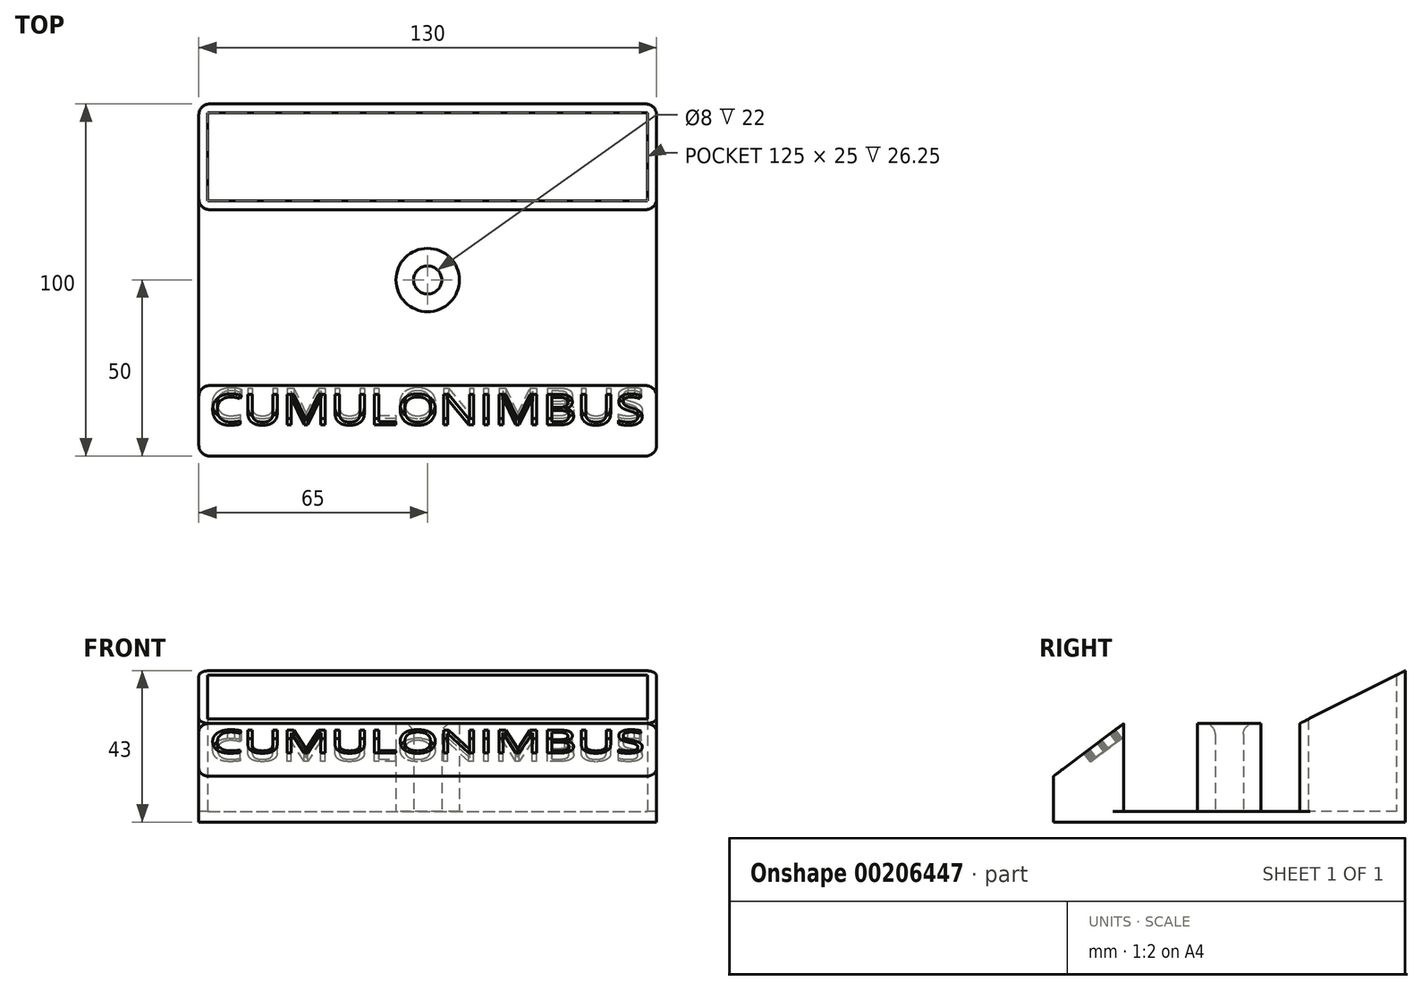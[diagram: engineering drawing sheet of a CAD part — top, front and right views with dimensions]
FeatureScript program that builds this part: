
annotation { "Feature Type Name" : "Feature", "Feature Type Description" : "" }
export const myFeature = defineFeature(function(context is Context, id is Id, definition is map)
    precondition{}
    {
        {
            var Q0;
            Q0=qCreatedBy(makeId("Top.planeOp"),FACE);
            var sketch = newSketch(context, id + "F0", { "sketchPlane" : qUnion([Q0])});
            skLineSegment(sketch, "E0.bottom", {"start": v(-65, 100) * mm, "end": v(65, 100) * mm});
            skLineSegment(sketch, "E0.top", {"start": v(-65, 0) * mm, "end": v(65, 0) * mm});
            skLineSegment(sketch, "E0.left", {"start": v(65, 100) * mm, "end": v(65, 0) * mm});
            skLineSegment(sketch, "E0.right", {"start": v(-65, 100) * mm, "end": v(-65, 0) * mm});
            skSolve(sketch);
        }
        {
            var Q0;
            Q0=makeQuery(id+"F0.imprint","IMPRINT",FACE,{"disambiguationData":[TD([[makeQuery(id+"F0.imprint","IMPRINT",EDGE,{"derivedFrom":sQuery(id+"F0.wireOp",EDGE,"E0.bottom")}),-1.0]])]});
            extrude(context, id + "F1", {"entities" : qUnion([Q0]), "depth" : 3 * mm});
        }
        {
            var Q0;
            Q0=makeQuery(id+"F1.opExtrude","CAP_FACE",FACE,{"disambiguationData":[OSD([sQuery(id+"F0.wireOp",EDGE,"E0.bottom"),sQuery(id+"F0.wireOp",EDGE,"E0.top"),sQuery(id+"F0.wireOp",EDGE,"E0.left"),sQuery(id+"F0.wireOp",EDGE,"E0.right")])],"isStart":false});
            var sketch = newSketch(context, id + "F2", { "sketchPlane" : qUnion([Q0])});
            skLineSegment(sketch, "E1", {"start": v(0, 0) * mm, "end": v(0, 100) * mm, "construction": true});
            skCircle(sketch, "E2", {"center": v(0, 50) * mm, "radius": 9 * mm});
            skCircle(sketch, "E3", {"center": v(0, 50) * mm, "radius": 4 * mm});
            skLineSegment(sketch, "E4.bottom", {"start": v(-65, 0) * mm, "end": v(65, 0) * mm});
            skLineSegment(sketch, "E4.top", {"start": v(-65, 20) * mm, "end": v(65, 20) * mm});
            skLineSegment(sketch, "E4.left", {"start": v(-65, 0) * mm, "end": v(-65, 20) * mm});
            skLineSegment(sketch, "E4.right", {"start": v(65, 0) * mm, "end": v(65, 20) * mm});
            skLineSegment(sketch, "E5.bottom", {"start": v(-65, 100) * mm, "end": v(65, 100) * mm});
            skLineSegment(sketch, "E5.top", {"start": v(-65, 70) * mm, "end": v(65, 70) * mm});
            skLineSegment(sketch, "E5.left", {"start": v(-65, 100) * mm, "end": v(-65, 70) * mm});
            skLineSegment(sketch, "E5.right", {"start": v(65, 100) * mm, "end": v(65, 70) * mm});
            skLineSegment(sketch, "E6.0", {"start": v(62.5, 97.5) * mm, "end": v(62.5, 72.5) * mm});
            skLineSegment(sketch, "E6.1", {"start": v(-62.5, 97.5) * mm, "end": v(62.5, 97.5) * mm});
            skLineSegment(sketch, "E6.2", {"start": v(-62.5, 97.5) * mm, "end": v(-62.5, 72.5) * mm});
            skLineSegment(sketch, "E6.3", {"start": v(-62.5, 72.5) * mm, "end": v(62.5, 72.5) * mm});
            skSolve(sketch);
        }
        {
            var Q0;
            Q0=makeQuery(id+"F2.imprint","IMPRINT",FACE,{"disambiguationData":[TD([[makeQuery(id+"F2.imprint","IMPRINT",EDGE,{"derivedFrom":sQuery(id+"F2.wireOp",EDGE,"E5.bottom")}),-1.0]])]});
            extrude(context, id + "F3", {"entities" : qUnion([Q0]), "operationType" : NewBodyOperationType.ADD, "depth" : 40 * mm});
        }
        {
            var Q0;
            Q0=makeQuery(id+"F2.imprint","IMPRINT",FACE,{"disambiguationData":[TD([[makeQuery(id+"F2.imprint","IMPRINT",EDGE,{"derivedFrom":sQuery(id+"F2.wireOp",EDGE,"E2")}),1.0]])]});
            var Q1;
            Q1=makeQuery(id+"F2.imprint","IMPRINT",FACE,{"disambiguationData":[TD([[makeQuery(id+"F2.imprint","IMPRINT",EDGE,{"derivedFrom":sQuery(id+"F2.wireOp",EDGE,"E4.bottom")}),1.0]])]});
            extrude(context, id + "F4", {"entities" : qUnion([Q0, Q1]), "operationType" : NewBodyOperationType.ADD, "depth" : 25 * mm});
        }
        {
            var Q0;
            Q0=makeQuery(id+"F4.opExtrude","CAP_EDGE",EDGE,{"disambiguationData":[OSD([sQuery(id+"F2.wireOp",EDGE,"E4.bottom")])],"isStart":false});
            chamfer(context, id + "F5", {"entities" : qUnion([Q0]), "chamferType" : ChamferType.TWO_OFFSETS, "width1" : 20 * mm, "oppositeDirection" : false, "width2" : 15 * mm, "tangentPropagation" : true});
        }
        {
            var Q0;
            Q0=makeQuery(id+"F3.opExtrude","CAP_EDGE",EDGE,{"disambiguationData":[OSD([sQuery(id+"F2.wireOp",EDGE,"E5.top")])],"isStart":false});
            chamfer(context, id + "F6", {"entities" : qUnion([Q0]), "chamferType" : ChamferType.TWO_OFFSETS, "width1" : 30 * mm, "oppositeDirection" : false, "width2" : 15 * mm, "tangentPropagation" : true});
        }
        {
            var Q0;
            Q0=makeQuery(id+"F3.boolean.opBoolean","MERGE",EDGE,{"derivedFrom":[makeQuery(id+"F1.opExtrude","SWEPT_EDGE",EDGE,{"disambiguationData":[OSD([sQuery(id+"F0.wireOp",EDGE,"E0.bottom"),sQuery(id+"F0.wireOp",EDGE,"E0.right")])]}),makeQuery(id+"F3.opExtrude","SWEPT_EDGE",EDGE,{"disambiguationData":[OSD([sQuery(id+"F2.wireOp",EDGE,"E5.bottom"),sQuery(id+"F2.wireOp",EDGE,"E5.left")])]})]});
            var Q1;
            Q1=makeQuery(id+"F3.opExtrude","SWEPT_EDGE",EDGE,{"disambiguationData":[OSD([sQuery(id+"F0.wireOp",EDGE,"E0.right"),sQuery(id+"F2.wireOp",EDGE,"E5.top"),sQuery(id+"F2.wireOp",EDGE,"E5.left")])]});
            var Q2;
            Q2=makeQuery(id+"F3.opExtrude","SWEPT_EDGE",EDGE,{"disambiguationData":[OSD([sQuery(id+"F0.wireOp",EDGE,"E0.left"),sQuery(id+"F2.wireOp",EDGE,"E5.top"),sQuery(id+"F2.wireOp",EDGE,"E5.right")])]});
            var Q3;
            Q3=makeQuery(id+"F4.boolean.opBoolean","MERGE",EDGE,{"derivedFrom":[makeQuery(id+"F1.opExtrude","SWEPT_EDGE",EDGE,{"disambiguationData":[OSD([sQuery(id+"F0.wireOp",EDGE,"E0.top"),sQuery(id+"F0.wireOp",EDGE,"E0.right")])]}),makeQuery(id+"F4.opExtrude","SWEPT_EDGE",EDGE,{"disambiguationData":[OSD([sQuery(id+"F2.wireOp",EDGE,"E4.bottom"),sQuery(id+"F2.wireOp",EDGE,"E4.left")])]})]});
            var Q4;
            Q4=makeQuery(id+"F3.boolean.opBoolean","MERGE",EDGE,{"derivedFrom":[makeQuery(id+"F1.opExtrude","SWEPT_EDGE",EDGE,{"disambiguationData":[OSD([sQuery(id+"F0.wireOp",EDGE,"E0.bottom"),sQuery(id+"F0.wireOp",EDGE,"E0.left")])]}),makeQuery(id+"F3.opExtrude","SWEPT_EDGE",EDGE,{"disambiguationData":[OSD([sQuery(id+"F2.wireOp",EDGE,"E5.bottom"),sQuery(id+"F2.wireOp",EDGE,"E5.right")])]})]});
            var Q5;
            Q5=makeQuery(id+"F4.boolean.opBoolean","MERGE",EDGE,{"derivedFrom":[makeQuery(id+"F1.opExtrude","SWEPT_EDGE",EDGE,{"disambiguationData":[OSD([sQuery(id+"F0.wireOp",EDGE,"E0.top"),sQuery(id+"F0.wireOp",EDGE,"E0.left")])]}),makeQuery(id+"F4.opExtrude","SWEPT_EDGE",EDGE,{"disambiguationData":[OSD([sQuery(id+"F2.wireOp",EDGE,"E4.bottom"),sQuery(id+"F2.wireOp",EDGE,"E4.right")])]})]});
            var Q6;
            Q6=makeQuery(id+"F4.opExtrude","SWEPT_EDGE",EDGE,{"disambiguationData":[OSD([sQuery(id+"F0.wireOp",EDGE,"E0.left"),sQuery(id+"F2.wireOp",EDGE,"E4.top"),sQuery(id+"F2.wireOp",EDGE,"E4.right")])]});
            var Q7;
            Q7=makeQuery(id+"F4.opExtrude","SWEPT_EDGE",EDGE,{"disambiguationData":[OSD([sQuery(id+"F0.wireOp",EDGE,"E0.right"),sQuery(id+"F2.wireOp",EDGE,"E4.top"),sQuery(id+"F2.wireOp",EDGE,"E4.left")])]});
            var Q8;
            Q8=makeQuery(id+"F4.opExtrude","CAP_EDGE",EDGE,{"disambiguationData":[OSD([sQuery(id+"F2.wireOp",EDGE,"E3")])],"isStart":false});
            fillet(context, id + "F7", {"entities" : qUnion([Q0, Q1, Q2, Q3, Q4, Q5, Q6, Q7, Q8]), "radius" : 3 * mm, "tangentPropagation" : true, "allowEdgeOverflow" : false});
        }
        {
            var Q0;
            Q0=makeQuery(id+"F5.opChamfer","BLEND_FACE",FACE,{"disambiguationData":[OSD([sQuery(id+"F2.wireOp",EDGE,"E4.bottom")])]});
            var sketch = newSketch(context, id + "F8", { "sketchPlane" : qUnion([Q0])});
            skLineSegment(sketch, "E7.0", {"start": v(62, 10.8) * mm, "end": v(-62, 10.8) * mm});
            skLineSegment(sketch, "E8.0", {"start": v(-62, 29.8) * mm, "end": v(62, 29.8) * mm});
            skText(sketch, "E9", { "text": "CUMULONIMBUS", "fontName": "OpenSans-Regular.ttf"});
            skLineSegment(sketch, "E10", {"start": v(-62, 10.8) * mm, "end": v(-62, 47.82) * mm});
            skLineSegment(sketch, "E11", {"start": v(62, 10.8) * mm, "end": v(62, 49.07) * mm});
            skPoint(sketch, "E11.endSnap0", {"position": v(62, 15.3) * mm});
            const initialGuessF8  = {"E9": [-0.062, 0.01887, 1, 0, 0.01093]};
            skSetInitialGuess(sketch, initialGuessF8);
            skSolve(sketch);
        }
        {
            var Q0;
            Q0=makeQuery(id+"F8.imprint","IMPRINT",FACE,{"disambiguationData":[TD([[makeQuery(id+"F8.imprint","IMPRINT",EDGE,{"derivedFrom":sQuery(id+"F8.wireOp",EDGE,"E9.sketch_text.stroke-0")}),-1.0]])]});
            var Q1;
            Q1=makeQuery(id+"F8.imprint","IMPRINT",FACE,{"disambiguationData":[TD([[makeQuery(id+"F8.imprint","IMPRINT",EDGE,{"derivedFrom":sQuery(id+"F8.wireOp",EDGE,"E9.sketch_text.stroke-13")}),-1.0]])]});
            var Q2;
            Q2=makeQuery(id+"F8.imprint","IMPRINT",FACE,{"disambiguationData":[TD([[makeQuery(id+"F8.imprint","IMPRINT",EDGE,{"derivedFrom":sQuery(id+"F8.wireOp",EDGE,"E9.sketch_text.stroke-19")}),-1.0]])]});
            var Q3;
            Q3=makeQuery(id+"F8.imprint","IMPRINT",FACE,{"disambiguationData":[TD([[makeQuery(id+"F8.imprint","IMPRINT",EDGE,{"derivedFrom":sQuery(id+"F8.wireOp",EDGE,"E9.sketch_text.stroke-27")}),-1.0]])]});
            var Q4;
            Q4=makeQuery(id+"F8.imprint","IMPRINT",FACE,{"disambiguationData":[TD([[makeQuery(id+"F8.imprint","IMPRINT",EDGE,{"derivedFrom":sQuery(id+"F8.wireOp",EDGE,"E9.sketch_text.stroke-43")}),-1.0]])]});
            var Q5;
            Q5=makeQuery(id+"F8.imprint","IMPRINT",FACE,{"disambiguationData":[TD([[makeQuery(id+"F8.imprint","IMPRINT",EDGE,{"derivedFrom":sQuery(id+"F8.wireOp",EDGE,"E9.sketch_text.stroke-58")}),-1.0]])]});
            var Q6;
            Q6=makeQuery(id+"F8.imprint","IMPRINT",FACE,{"disambiguationData":[TD([[makeQuery(id+"F8.imprint","IMPRINT",EDGE,{"derivedFrom":sQuery(id+"F8.wireOp",EDGE,"E9.sketch_text.stroke-72")}),-1.0]])]});
            var Q7;
            Q7=makeQuery(id+"F8.imprint","IMPRINT",FACE,{"disambiguationData":[TD([[makeQuery(id+"F8.imprint","IMPRINT",EDGE,{"derivedFrom":sQuery(id+"F8.wireOp",EDGE,"E9.sketch_text.stroke-90")}),-1.0]])]});
            var Q8;
            Q8=makeQuery(id+"F8.imprint","IMPRINT",FACE,{"disambiguationData":[TD([[makeQuery(id+"F8.imprint","IMPRINT",EDGE,{"derivedFrom":sQuery(id+"F8.wireOp",EDGE,"E9.sketch_text.stroke-104")}),-1.0]])]});
            var Q9;
            Q9=makeQuery(id+"F8.imprint","IMPRINT",FACE,{"disambiguationData":[TD([[makeQuery(id+"F8.imprint","IMPRINT",EDGE,{"derivedFrom":sQuery(id+"F8.wireOp",EDGE,"E9.sketch_text.stroke-110")}),-1.0]])]});
            var Q10;
            Q10=makeQuery(id+"F8.imprint","IMPRINT",FACE,{"disambiguationData":[TD([[makeQuery(id+"F8.imprint","IMPRINT",EDGE,{"derivedFrom":sQuery(id+"F8.wireOp",EDGE,"E9.sketch_text.stroke-124")}),-1.0]])]});
            var Q11;
            Q11=makeQuery(id+"F8.imprint","IMPRINT",FACE,{"disambiguationData":[TD([[makeQuery(id+"F8.imprint","IMPRINT",EDGE,{"derivedFrom":sQuery(id+"F8.wireOp",EDGE,"E9.sketch_text.stroke-67")}),-1.0]])]});
            var Q12;
            Q12=makeQuery(id+"F8.imprint","IMPRINT",FACE,{"disambiguationData":[TD([[makeQuery(id+"F8.imprint","IMPRINT",EDGE,{"derivedFrom":sQuery(id+"F8.wireOp",EDGE,"E9.sketch_text.stroke-61")}),-1.0]])]});
            var Q13;
            Q13=makeQuery(id+"F8.imprint","IMPRINT",FACE,{"disambiguationData":[TD([[makeQuery(id+"F8.imprint","IMPRINT",EDGE,{"derivedFrom":sQuery(id+"F8.wireOp",EDGE,"E9.sketch_text.stroke-98")}),-1.0]])]});
            var Q14;
            Q14=makeQuery(id+"F8.imprint","IMPRINT",FACE,{"disambiguationData":[TD([[makeQuery(id+"F8.imprint","IMPRINT",EDGE,{"derivedFrom":sQuery(id+"F8.wireOp",EDGE,"E9.sketch_text.stroke-145")}),-1.0]])]});
            var Q15;
            Q15=makeQuery(id+"F8.imprint","IMPRINT",FACE,{"disambiguationData":[TD([[makeQuery(id+"F8.imprint","IMPRINT",EDGE,{"derivedFrom":sQuery(id+"F8.wireOp",EDGE,"E9.sketch_text.stroke-159")}),-1.0]])]});
            extrude(context, id + "F9", {"entities" : qUnion([Q0, Q1, Q2, Q3, Q4, Q5, Q6, Q7, Q8, Q9, Q10, Q11, Q12, Q13, Q14, Q15]), "operationType" : NewBodyOperationType.REMOVE, "oppositeDirection" : true, "depth" : 3 * mm});
        }
    });
